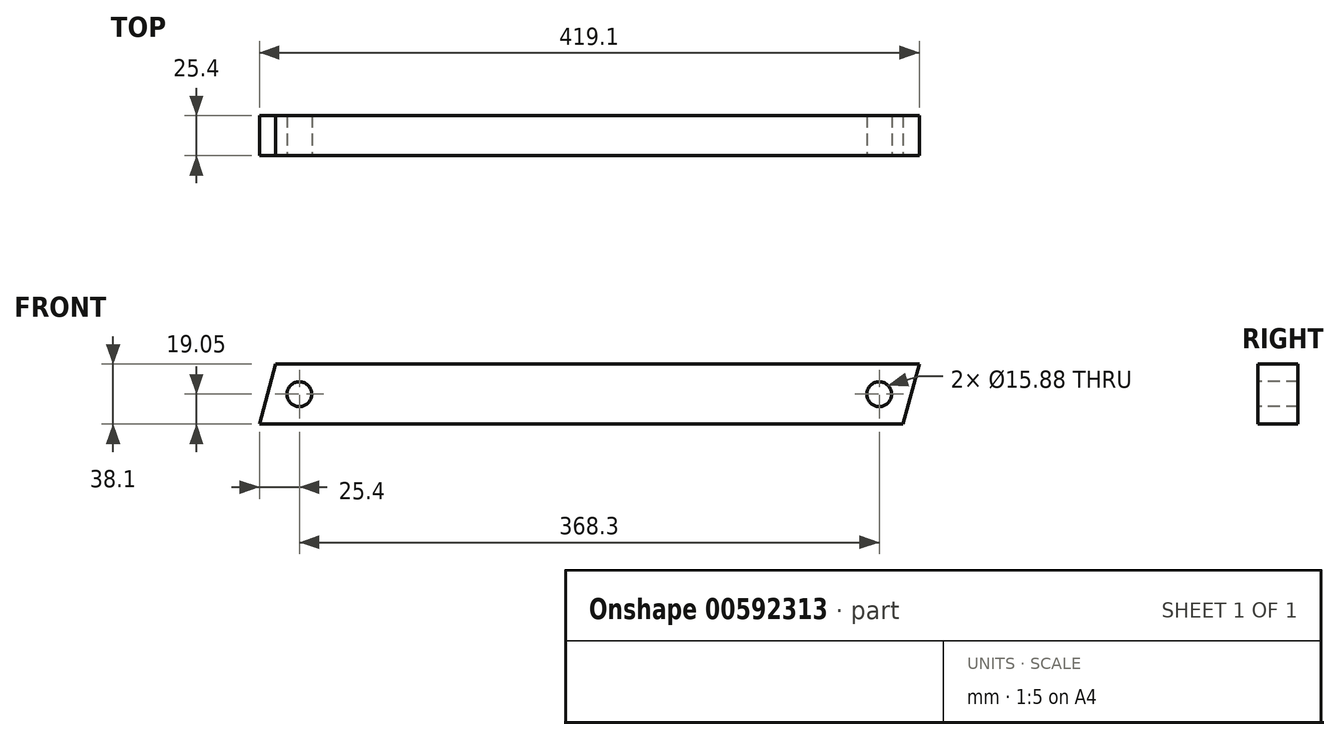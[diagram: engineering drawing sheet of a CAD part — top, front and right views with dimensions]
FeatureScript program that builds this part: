
annotation { "Feature Type Name" : "Feature", "Feature Type Description" : "" }
export const myFeature = defineFeature(function(context is Context, id is Id, definition is map)
    precondition{}
    {
        {
            var Q0;
            Q0=qCreatedBy(makeId("Front.planeOp"),FACE);
            var sketch = newSketch(context, id + "F0", { "sketchPlane" : qUnion([Q0])});
            skLineSegment(sketch, "E0.bottom", {"start": v(0, 0) * mm, "end": v(419.1, 0) * mm});
            skLineSegment(sketch, "E0.top", {"start": v(0, 38.1) * mm, "end": v(419.1, 38.1) * mm});
            skLineSegment(sketch, "E0.left", {"start": v(0, 0) * mm, "end": v(0, 38.1) * mm});
            skLineSegment(sketch, "E0.right", {"start": v(419.1, 0) * mm, "end": v(419.1, 38.1) * mm});
            skSolve(sketch);
        }
        {
            var Q0;
            Q0=makeQuery(id+"F0.imprint","IMPRINT",FACE,{"disambiguationData":[TD([[makeQuery(id+"F0.imprint","IMPRINT",EDGE,{"derivedFrom":sQuery(id+"F0.wireOp",EDGE,"E0.bottom")}),1.0]])]});
            extrude(context, id + "F1", {"entities" : qUnion([Q0]), "depth" : 25.4 * mm, "offsetDistance" : 25.4 * mm});
        }
        {
            var Q0;
            Q0=makeQuery(id+"F1.opExtrude","CAP_FACE",FACE,{"disambiguationData":[OSD([sQuery(id+"F0.wireOp",EDGE,"E0.bottom"),sQuery(id+"F0.wireOp",EDGE,"E0.top"),sQuery(id+"F0.wireOp",EDGE,"E0.left"),sQuery(id+"F0.wireOp",EDGE,"E0.right")])],"isStart":false});
            var sketch = newSketch(context, id + "F2", { "sketchPlane" : qUnion([Q0])});
            skCircle(sketch, "E1", {"center": v(25.4, 19.05) * mm, "radius": 6.35 * mm});
            skCircle(sketch, "E2", {"center": v(393.7, 19.05) * mm, "radius": 6.35 * mm});
            skSolve(sketch);
        }
        {
            var Q0;
            Q0=sQuery(id+"F2.wireOp",VERTEX,"E1.center");
            var Q1;
            Q1=sQuery(id+"F2.wireOp",VERTEX,"1KIZwOIM-GRpi-KB8x-ajEx-Oq6Q15zxiPFI.center");
            var Q2;
            Q2=sQuery(id+"F2.wireOp",VERTEX,"Mo5Y4d3M-FWyN-rOX8-mSTb-Zg6RNz9Z2ruR.center");
            var Q3;
            Q3=sQuery(id+"F2.wireOp",VERTEX,"E2.center");
            var Q4;
            Q4=makeQuery(id+"F1.opExtrude","SWEPT_BODY",BODY,{"disambiguationData":[OSD([sQuery(id+"F0.wireOp",EDGE,"E0.bottom"),sQuery(id+"F0.wireOp",EDGE,"E0.top"),sQuery(id+"F0.wireOp",EDGE,"E0.left"),sQuery(id+"F0.wireOp",EDGE,"E0.right")])]});
            hole(context, id + "F3", {"style" : HoleStyle.SIMPLE, "endStyle" : HoleEndStyle.THROUGH, "holeDiameter" : 15.88 * mm, "majorDiameter" : 6.35 * mm, "isTappedThrough" : true, "tappedDepth" : 12.7 * mm, "tapClearance" : 3, "locations" : qUnion([Q0, Q1, Q2, Q3]), "scope" : qUnion([Q4])});
        }
        {
            var Q0;
            Q0=makeQuery(id+"F1.opExtrude","CAP_FACE",FACE,{"disambiguationData":[OSD([sQuery(id+"F0.wireOp",EDGE,"E0.bottom"),sQuery(id+"F0.wireOp",EDGE,"E0.top"),sQuery(id+"F0.wireOp",EDGE,"E0.left"),sQuery(id+"F0.wireOp",EDGE,"E0.right")])],"isStart":false});
            var sketch = newSketch(context, id + "F4", { "sketchPlane" : qUnion([Q0])});
            skLineSegment(sketch, "E3", {"start": v(0, 0) * mm, "end": v(10.2, 38.1) * mm});
            skLineSegment(sketch, "E4", {"start": v(10.2, 38.1) * mm, "end": v(0, 38.1) * mm});
            skLineSegment(sketch, "E5", {"start": v(0, 38.1) * mm, "end": v(0, 0) * mm});
            skSolve(sketch);
        }
        {
            var Q0;
            Q0=makeQuery(id+"F4.imprint","IMPRINT",FACE,{"disambiguationData":[TD([[makeQuery(id+"F4.imprint","IMPRINT",EDGE,{"derivedFrom":sQuery(id+"F4.wireOp",EDGE,"E3")}),1.0]])]});
            extrude(context, id + "F5", {"entities" : qUnion([Q0]), "operationType" : NewBodyOperationType.REMOVE, "oppositeDirection" : true, "depth" : 50.8 * mm, "offsetDistance" : 25.4 * mm});
        }
        {
            var Q0;
            Q0=makeQuery(id+"F1.opExtrude","CAP_FACE",FACE,{"disambiguationData":[OSD([sQuery(id+"F0.wireOp",EDGE,"E0.bottom"),sQuery(id+"F0.wireOp",EDGE,"E0.top"),sQuery(id+"F0.wireOp",EDGE,"E0.left"),sQuery(id+"F0.wireOp",EDGE,"E0.right")])],"isStart":false});
            var sketch = newSketch(context, id + "F6", { "sketchPlane" : qUnion([Q0])});
            skLineSegment(sketch, "E6", {"start": v(419.1, 38.1) * mm, "end": v(408.9, 0) * mm});
            skLineSegment(sketch, "E7", {"start": v(408.9, 0) * mm, "end": v(419.1, 0) * mm});
            skLineSegment(sketch, "E8", {"start": v(419.1, 0) * mm, "end": v(419.1, 38.1) * mm});
            skSolve(sketch);
        }
        {
            var Q0;
            Q0=makeQuery(id+"F6.imprint","IMPRINT",FACE,{"disambiguationData":[TD([[makeQuery(id+"F6.imprint","IMPRINT",EDGE,{"derivedFrom":sQuery(id+"F6.wireOp",EDGE,"E6")}),1.0]])]});
            extrude(context, id + "F7", {"entities" : qUnion([Q0]), "operationType" : NewBodyOperationType.REMOVE, "oppositeDirection" : true, "depth" : 50.8 * mm, "offsetDistance" : 25.4 * mm});
        }
    });
